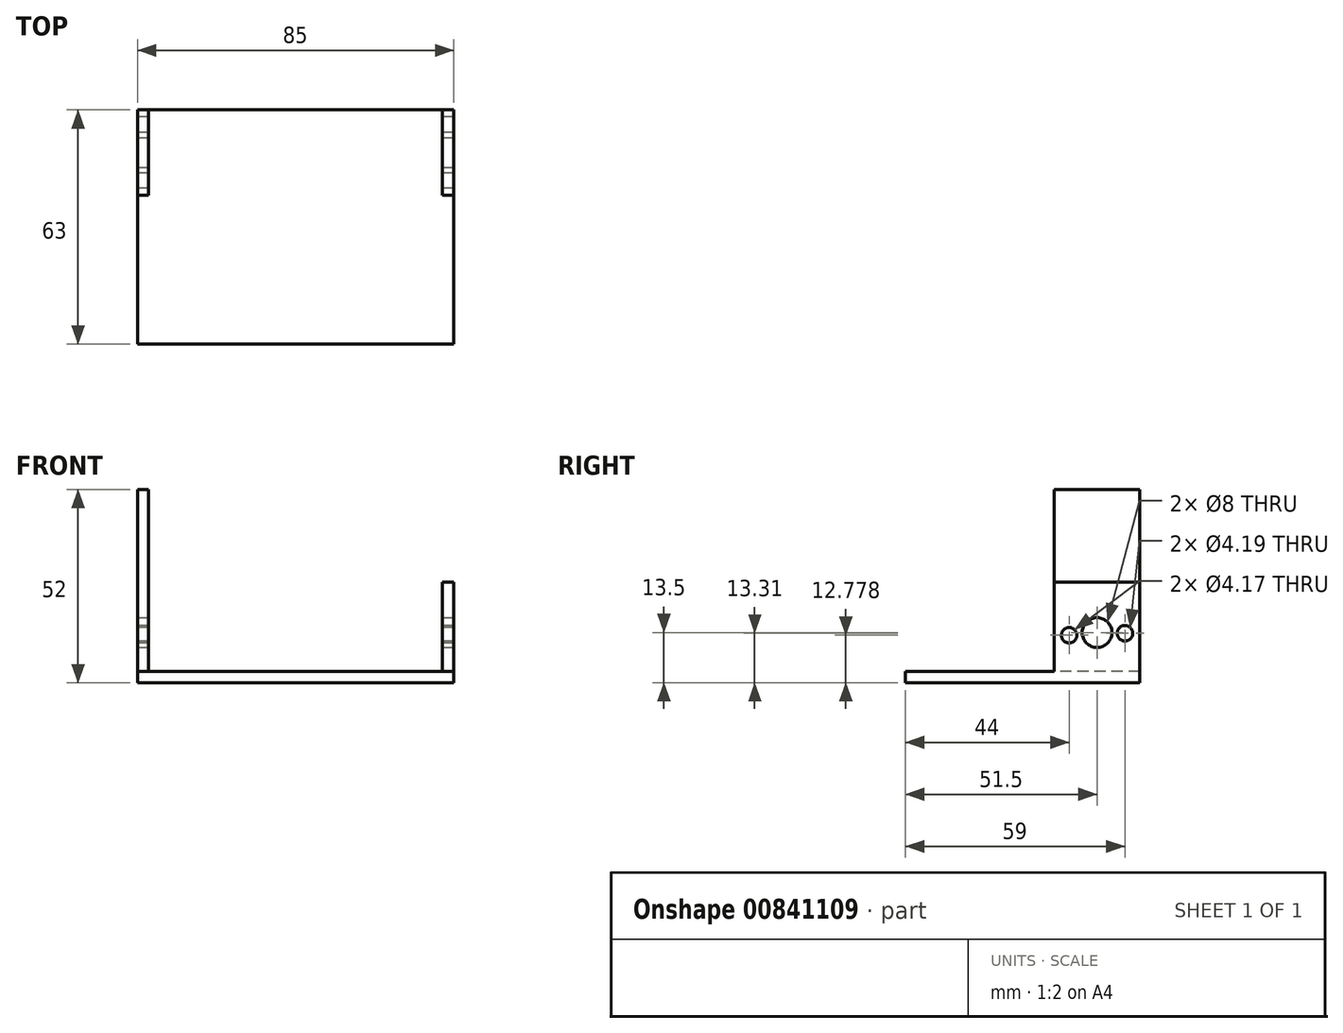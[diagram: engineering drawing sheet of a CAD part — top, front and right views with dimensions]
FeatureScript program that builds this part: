
annotation { "Feature Type Name" : "Feature", "Feature Type Description" : "" }
export const myFeature = defineFeature(function(context is Context, id is Id, definition is map)
    precondition{}
    {
        {
            var Q0;
            Q0=qCreatedBy(makeId("Top.planeOp"),FACE);
            var sketch = newSketch(context, id + "F0", { "sketchPlane" : qUnion([Q0])});
            skLineSegment(sketch, "E0.bottom", {"start": v(0, 0) * mm, "end": v(85, 0) * mm});
            skLineSegment(sketch, "E0.top", {"start": v(0, 23) * mm, "end": v(85, 23) * mm});
            skLineSegment(sketch, "E0.left", {"start": v(0, 0) * mm, "end": v(0, 23) * mm});
            skLineSegment(sketch, "E0.right", {"start": v(85, 0) * mm, "end": v(85, 23) * mm});
            skLineSegment(sketch, "E1.top", {"start": v(0, -40) * mm, "end": v(85, -40) * mm});
            skLineSegment(sketch, "E1.left", {"start": v(0, 0) * mm, "end": v(0, -40) * mm});
            skLineSegment(sketch, "E1.right", {"start": v(85, 0) * mm, "end": v(85, -40) * mm});
            skSolve(sketch);
        }
        {
            var Q0;
            Q0=qSketchRegion(id+"F0",true);
            extrude(context, id + "F1", {"entities" : qUnion([Q0]), "depth" : 3 * mm, "offsetDistance" : 25 * mm});
        }
        {
            var Q0;
            Q0=makeQuery(id+"F1.opExtrude","CAP_FACE",FACE,{"disambiguationData":[OSD([sQuery(id+"F0.wireOp",EDGE,"E0.bottom"),sQuery(id+"F0.wireOp",EDGE,"E0.top"),sQuery(id+"F0.wireOp",EDGE,"E0.left"),sQuery(id+"F0.wireOp",EDGE,"E0.right")])],"isStart":false});
            var sketch = newSketch(context, id + "F2", { "sketchPlane" : qUnion([Q0])});
            skLineSegment(sketch, "E2.bottom", {"start": v(0, 23) * mm, "end": v(3, 23) * mm});
            skLineSegment(sketch, "E2.top", {"start": v(0, 0) * mm, "end": v(3, 0) * mm});
            skLineSegment(sketch, "E2.left", {"start": v(0, 23) * mm, "end": v(0, 0) * mm});
            skLineSegment(sketch, "E2.right", {"start": v(3, 23) * mm, "end": v(3, 0) * mm});
            skLineSegment(sketch, "E3.bottom", {"start": v(85, 23) * mm, "end": v(82, 23) * mm});
            skLineSegment(sketch, "E3.top", {"start": v(85, 0) * mm, "end": v(82, 0) * mm});
            skLineSegment(sketch, "E3.left", {"start": v(85, 23) * mm, "end": v(85, 0) * mm});
            skLineSegment(sketch, "E3.right", {"start": v(82, 23) * mm, "end": v(82, 0) * mm});
            skSolve(sketch);
        }
        {
            var Q0;
            Q0=qSketchRegion(id+"F2",true);
            extrude(context, id + "F3", {"entities" : qUnion([Q0]), "operationType" : NewBodyOperationType.ADD, "depth" : 24 * mm, "offsetDistance" : 25 * mm});
        }
        {
            var Q0;
            Q0=makeQuery(id+"F3.opExtrude","CAP_FACE",FACE,{"disambiguationData":[OSD([sQuery(id+"F2.wireOp",EDGE,"E2.bottom"),sQuery(id+"F2.wireOp",EDGE,"E2.top"),sQuery(id+"F2.wireOp",EDGE,"E2.left"),sQuery(id+"F2.wireOp",EDGE,"E2.right")])],"isStart":false});
            var sketch = newSketch(context, id + "F4", { "sketchPlane" : qUnion([Q0])});
            skLineSegment(sketch, "E4.bottom", {"start": v(0, 23) * mm, "end": v(3, 23) * mm});
            skLineSegment(sketch, "E4.top", {"start": v(0, 0) * mm, "end": v(3, 0) * mm});
            skLineSegment(sketch, "E4.left", {"start": v(0, 23) * mm, "end": v(0, 0) * mm});
            skLineSegment(sketch, "E4.right", {"start": v(3, 23) * mm, "end": v(3, 0) * mm});
            skSolve(sketch);
        }
        {
            var Q0;
            Q0=qSketchRegion(id+"F4",true);
            extrude(context, id + "F5", {"entities" : qUnion([Q0]), "operationType" : NewBodyOperationType.ADD, "depth" : 25 * mm, "offsetDistance" : 25 * mm});
        }
        {
            var Q0;
            Q0=makeQuery(id+"F3.boolean.opBoolean","MERGE",FACE,{"derivedFrom":[makeQuery(id+"F1.opExtrude","SWEPT_FACE",FACE,{"disambiguationData":[OSD([sQuery(id+"F0.wireOp",EDGE,"E0.right"),sQuery(id+"F0.wireOp",EDGE,"E1.right")])]}),makeQuery(id+"F3.opExtrude","SWEPT_FACE",FACE,{"disambiguationData":[OSD([sQuery(id+"F2.wireOp",EDGE,"E3.left")])]})]});
            var sketch = newSketch(context, id + "F6", { "sketchPlane" : qUnion([Q0])});
            skLineSegment(sketch, "E5", {"start": v(0, 27) * mm, "end": v(23, 0) * mm, "construction": true});
            skLineSegment(sketch, "E6", {"start": v(23, 0) * mm, "end": v(23, 27) * mm, "construction": true});
            skLineSegment(sketch, "E7", {"start": v(23, 27) * mm, "end": v(0, 0) * mm, "construction": true});
            skCircle(sketch, "E8", {"center": v(11.5, 13.5) * mm, "radius": 4 * mm});
            skSolve(sketch);
        }
        {
            var Q0;
            Q0=qSketchRegion(id+"F6",true);
            extrude(context, id + "F7", {"entities" : qUnion([Q0]), "operationType" : NewBodyOperationType.REMOVE, "oppositeDirection" : true, "depth" : 200 * mm, "offsetDistance" : 25 * mm});
        }
        {
            var Q0;
            Q0=qCreatedBy(makeId("Right.planeOp"),FACE);
            var sketch = newSketch(context, id + "F8", { "sketchPlane" : qUnion([Q0])});
            skPoint(sketch, "E9", {"position": v(11.65, 13.3) * mm});
            skPoint(sketch, "E10.orphan", {"position": v(0, 26.76) * mm});
            skPoint(sketch, "E11.end.orphan", {"position": v(23.17, 0) * mm});
            skPoint(sketch, "E12", {"position": v(8, 13.3) * mm});
            skPoint(sketch, "E13", {"position": v(15, 13.3) * mm});
            skCircle(sketch, "E14", {"center": v(19, 13.3) * mm, "radius": 2.1 * mm});
            skPoint(sketch, "E15.trimOffspring.end.orphan", {"position": v(23, 13.3) * mm});
            skPoint(sketch, "E16.end.orphan", {"position": v(0, 13.3) * mm});
            skSolve(sketch);
        }
        {
            var Q0;
            Q0=makeQuery(id+"F8.imprint","IMPRINT",FACE,{"disambiguationData":[TD([[makeQuery(id+"F8.imprint","IMPRINT",EDGE,{"derivedFrom":sQuery(id+"F8.wireOp",EDGE,"E14")}),1.0]])]});
            extrude(context, id + "F9", {"entities" : qUnion([Q0]), "operationType" : NewBodyOperationType.REMOVE, "depth" : 101.9 * mm, "offsetDistance" : 25 * mm});
        }
        {
            var Q0;
            Q0=qCreatedBy(makeId("Right.planeOp"),FACE);
            var sketch = newSketch(context, id + "F10", { "sketchPlane" : qUnion([Q0])});
            skPoint(sketch, "E17", {"position": v(4, 12.78) * mm});
            skCircle(sketch, "E18", {"center": v(4, 12.78) * mm, "radius": 2.09 * mm});
            skPoint(sketch, "E19.orphan", {"position": v(0, 12.78) * mm});
            skSolve(sketch);
        }
        {
            var Q0;
            Q0 = qSketchRegion(id + "F10", true);
            extrude(context, id + "F11", {"entities" : qUnion([Q0]), "operationType" : NewBodyOperationType.REMOVE, "depth" : 136.8 * mm, "offsetDistance" : 25 * mm});
        }
    });
